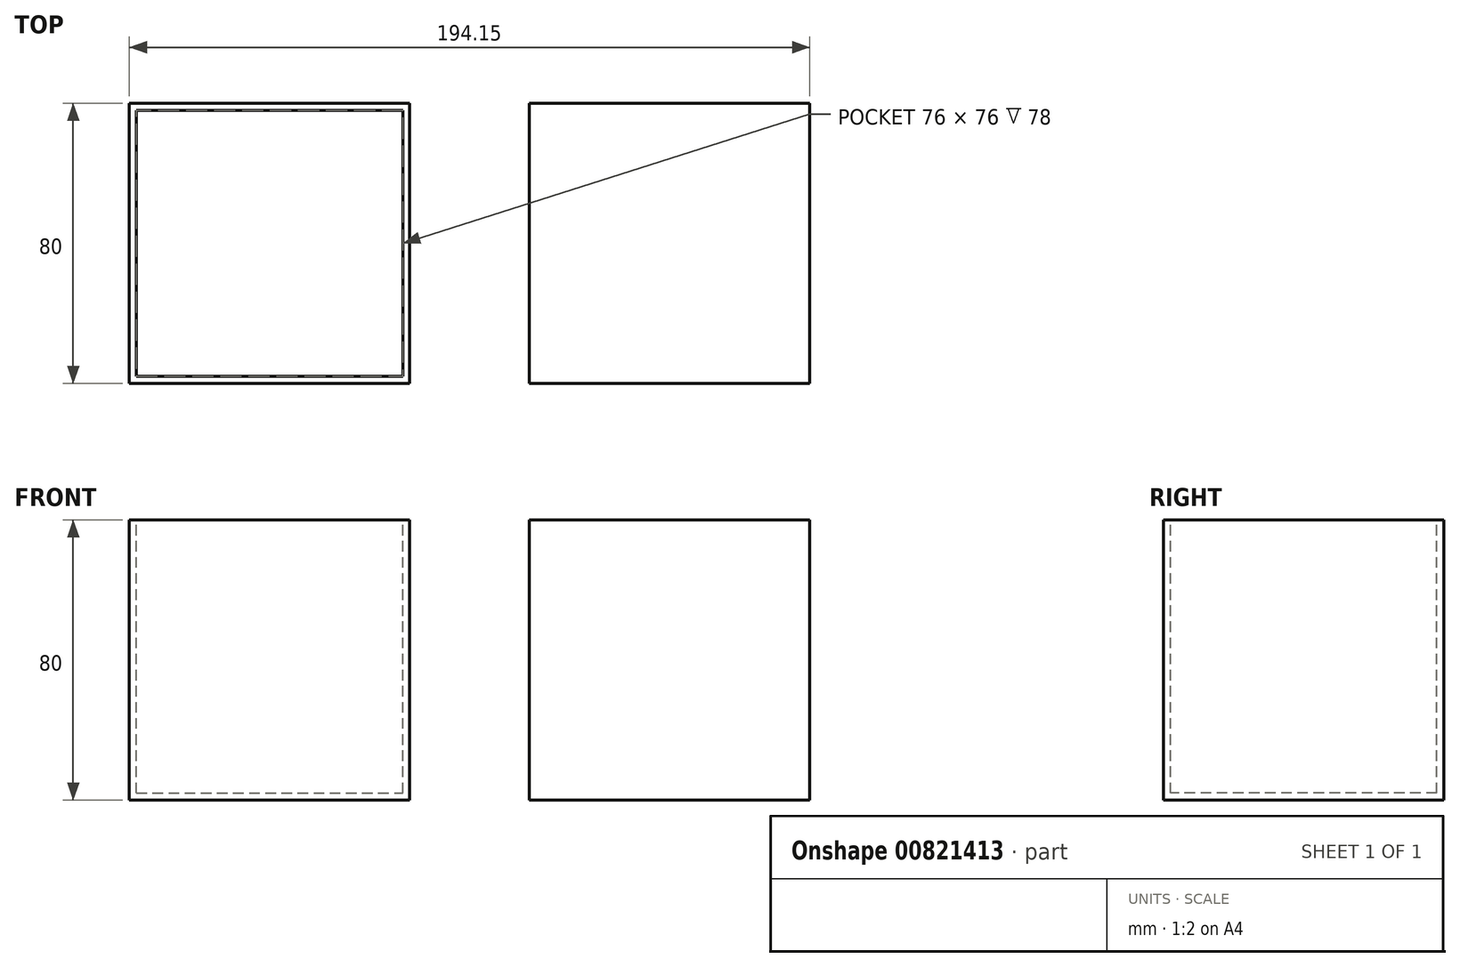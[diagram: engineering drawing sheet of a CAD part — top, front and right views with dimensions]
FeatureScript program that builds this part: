
annotation { "Feature Type Name" : "Feature", "Feature Type Description" : "" }
export const myFeature = defineFeature(function(context is Context, id is Id, definition is map)
    precondition{}
    {
        {
            var Q0;
            Q0=qCreatedBy(makeId("Top.planeOp"),FACE);
            var sketch = newSketch(context, id + "F0", { "sketchPlane" : qUnion([Q0])});
            skLineSegment(sketch, "E0.bottom", {"start": v(-133.95, 40.16) * mm, "end": v(-53.95, 40.16) * mm});
            skLineSegment(sketch, "E0.top", {"start": v(-133.95, -39.84) * mm, "end": v(-53.95, -39.84) * mm});
            skLineSegment(sketch, "E0.left", {"start": v(-133.95, 40.16) * mm, "end": v(-133.95, -39.84) * mm});
            skLineSegment(sketch, "E0.right", {"start": v(-53.95, 40.16) * mm, "end": v(-53.95, -39.84) * mm});
            skPoint(sketch, "E1.oppositeSnap0", {"position": v(-93.95, 40.16) * mm});
            skLineSegment(sketch, "E1.bottom", {"start": v(-19.8, -39.84) * mm, "end": v(60.2, -39.84) * mm});
            skLineSegment(sketch, "E1.top", {"start": v(-19.8, 40.16) * mm, "end": v(60.2, 40.16) * mm});
            skLineSegment(sketch, "E1.left", {"start": v(-19.8, -39.84) * mm, "end": v(-19.8, 40.16) * mm});
            skLineSegment(sketch, "E1.right", {"start": v(60.2, -39.84) * mm, "end": v(60.2, 40.16) * mm});
            skSolve(sketch);
        }
        {
            var Q0;
            Q0=makeQuery(id+"F0.imprint","IMPRINT",FACE,{"disambiguationData":[TD([[makeQuery(id+"F0.imprint","IMPRINT",EDGE,{"derivedFrom":sQuery(id+"F0.wireOp",EDGE,"E0.bottom")}),-1.0]])]});
            extrude(context, id + "F1", {"entities" : qUnion([Q0]), "depth" : 80 * mm, "offsetDistance" : 25 * mm});
        }
        {
            var Q0;
            Q0=makeQuery(id+"F0.imprint","IMPRINT",FACE,{"disambiguationData":[TD([[makeQuery(id+"F0.imprint","IMPRINT",EDGE,{"derivedFrom":sQuery(id+"F0.wireOp",EDGE,"E1.bottom")}),1.0]])]});
            extrude(context, id + "F2", {"entities" : qUnion([Q0]), "depth" : 80 * mm, "offsetDistance" : 25 * mm});
        }
        {
            var Q0;
            Q0=makeQuery(id+"F1.opExtrude","CAP_FACE",FACE,{"disambiguationData":[OSD([sQuery(id+"F0.wireOp",EDGE,"E0.bottom"),sQuery(id+"F0.wireOp",EDGE,"E0.top"),sQuery(id+"F0.wireOp",EDGE,"E0.left"),sQuery(id+"F0.wireOp",EDGE,"E0.right")])],"isStart":false});
            var sketch = newSketch(context, id + "F3", { "sketchPlane" : qUnion([Q0])});
            skLineSegment(sketch, "E2.bottom", {"start": v(-131.95, 38.16) * mm, "end": v(-55.95, 38.16) * mm});
            skLineSegment(sketch, "E2.top", {"start": v(-131.95, -37.84) * mm, "end": v(-55.95, -37.84) * mm});
            skLineSegment(sketch, "E2.left", {"start": v(-131.95, 38.16) * mm, "end": v(-131.95, -37.84) * mm});
            skLineSegment(sketch, "E2.right", {"start": v(-55.95, 38.16) * mm, "end": v(-55.95, -37.84) * mm});
            skSolve(sketch);
        }
        {
            var Q0;
            Q0=makeQuery(id+"F3.imprint","IMPRINT",FACE,{"disambiguationData":[TD([[makeQuery(id+"F3.imprint","IMPRINT",EDGE,{"derivedFrom":sQuery(id+"F3.wireOp",EDGE,"E2.bottom")}),-1.0]])]});
            extrude(context, id + "F4", {"entities" : qUnion([Q0]), "oppositeDirection" : true, "depth" : 78 * mm, "offsetDistance" : 25 * mm});
        }
        {
            var Q0;
            Q0=makeQuery(id+"F4.opExtrude","SWEPT_BODY",BODY,{"disambiguationData":[OSD([sQuery(id+"F3.wireOp",EDGE,"E2.bottom"),sQuery(id+"F3.wireOp",EDGE,"E2.top"),sQuery(id+"F3.wireOp",EDGE,"E2.left"),sQuery(id+"F3.wireOp",EDGE,"E2.right")])]});
            var Q1;
            Q1=makeQuery(id+"F1.opExtrude","SWEPT_BODY",BODY,{"disambiguationData":[OSD([sQuery(id+"F0.wireOp",EDGE,"E0.bottom"),sQuery(id+"F0.wireOp",EDGE,"E0.top"),sQuery(id+"F0.wireOp",EDGE,"E0.left"),sQuery(id+"F0.wireOp",EDGE,"E0.right")])]});
            booleanBodies(context, id + "F5", {"operationType" : BooleanOperationType.SUBTRACTION, "tools" : qUnion([Q0]), "targets" : qUnion([Q1])});
        }
    });
